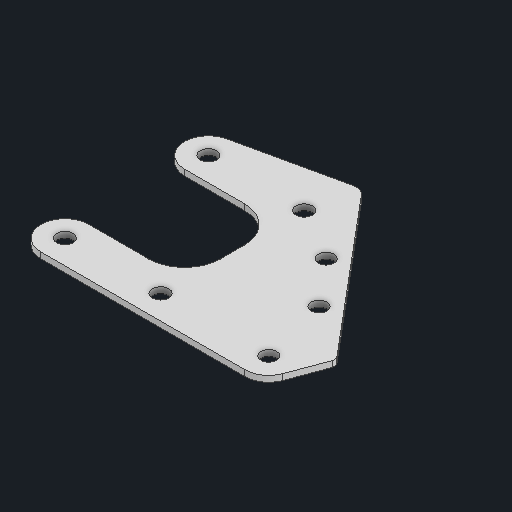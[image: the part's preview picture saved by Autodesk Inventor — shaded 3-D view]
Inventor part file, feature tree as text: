
AUTODESK INVENTOR PART (.ipt)
format: ipt  version: 2025 (Build 290162000, 162)  size: 147,456 bytes
history: native  units: in
note: dims shown in document units (in); Inventor stores cm internally (conversion verified against a paired STEP export)
features: other x6, sketch x1
ambient origin geometry x8: Origin, YZ Plane, XZ Plane, XY Plane, X Axis, Y Axis, Z Axis, Center Point
bodies: Solid1 (feature_tree)
feature tree (7):
  other  "funel_gusset.ipt"
  other  "Blocks"
  other  "main"
  other  "Solid1::funel_gusset.ipt"
  other  "TaggingFeature1"
  sketch  "Sketch1"  dims[d0=0.3937in d1=0.5in d6=0.375in d8=0.164in d9=0.0625in d14=0.164in d15=0.615in d17=0.125in]
  other  "main:1"
